# Revit family: ArmaGirt_Z-Girt
name_source: partatom
category: Specialty Equipment
units: mm (PartAtom-declared; Revit-internal decimal feet)

## family parameters
Cut with Voids When Loaded = No
Enable Cutting in Views = No
Host = Face
Maintain Annotation Orientation = No
Part Type = Normal
Room Calculation Point = No
Round Connector Dimension = Use Diameter
Shared = No

## types (5) — shared parameters
Assembly Code = B
AssetType = Fixed
BIMObjectName = Armadillo_StructuralThermalBreak_Armatherm_Z-Girt
ClassificationName = Uniclass2015
ClassificationValue = Pr_35_90_15_89
Default Elevation = 1200 mm
Density = 1.8-2.0 gr/cm³
Description = Armatherm thermally broken cladding support connection solutions prevent excessive heat flow and potential condensation problems otherwise associated with thermal bridging.
DocumentationCertificates = https://www.armatherm.co.uk
DocumentationInstallationGuide = https://www.armatherm.co.uk
DocumentationLiterature = https://www.bimstore.co
DocumentationMaintenance = https://www.armatherm.co.uk
DocumentationTechnical = https://www.bimstore.co
DurationUnit = Year
FlammabilityClassification = V0
FlexuralModulus = not less than 11035 MPa
FlexuralStrength = 230 MPa
IfcExportAs = IfcBuildingElementProxyType
IfcExportType = USERDEFINED
InnerRadius = 1.8 mm  [stored 0.00590551 ft]
Keynote = G
Manufacturer = Armadillo
ManufacturerName = Armadillo
Material = Thermoset resin
Model = Z-Girt
ModelNumber = Z-Girt
ModelReference = Structural thermal break
NBSDescription = Thermal break connection plates
NBSObjectName = Armadillo Thermal break connection plates
NBSReference = 45-75-42/399
OuterRadius = 4.6 mm  [stored 0.0150919 ft]
Product data url = https://www.bimobject.com
ProductionYear = 2020
StructuralThermalBreakMaterial = Armadillo_StructuralThermalBreak_Armatherm_Z-Girt
Type Comments = Structural thermal break
TypeName = Structural thermal break
URL = https://www.armatherm.co.uk
WarrantyDurationLabor = 0
WarrantyDurationParts = 0
WarrantyDurationUnit = Year
WaterAbsorption = 0.6% max
_BSBibleVersion = 16
_CurrentRevision = 1
_DistributedBy = www.bimstore.co
zero-valued in all types: ExpectedLife, _BimSpecGuid

## per-type parameters (varying)
| type | C | Depth | Height | NominalDepth | NominalHeight | Thickness |
| 38.1mm | 38 mm  [stored 0.124672 ft] | 38.1 mm  [stored 0.125 ft] | 72 mm | 38.1 mm  [stored 0.125 ft] | 4 mm  [stored 0.0131234 ft] | 4 mm  [stored 0.0131234 ft] |
| 50.8mm | 38 mm  [stored 0.124672 ft] | 50.8 mm  [stored 0.166667 ft] | 72 mm | 50.8 mm  [stored 0.166667 ft] | 4 mm  [stored 0.0131234 ft] | 4 mm  [stored 0.0131234 ft] |
| 63.5mm | 38 mm  [stored 0.124672 ft] | 63.5 mm | 72 mm | 63.5 mm | 4 mm  [stored 0.0131234 ft] | 4 mm  [stored 0.0131234 ft] |
| 76.2mm | 38 mm  [stored 0.124672 ft] | 76.2 mm  [stored 0.25 ft] | 72 mm | 76.2 mm  [stored 0.25 ft] | 4 mm  [stored 0.0131234 ft] | 4 mm  [stored 0.0131234 ft] |
| 101.6mm | 51 mm | 101.6 mm  [stored 0.333333 ft] | 97 mm | 101.6 mm  [stored 0.333333 ft] | 5 mm  [stored 0.0164042 ft] | 5 mm  [stored 0.0164042 ft] |

note: [stored X ft] marks values corroborated as IEEE doubles in the binary element streams (Revit-internal decimal feet)

## geometry (parser evidence)
native form markers: Sweep x2
no freeform markers — native parametric forms only
